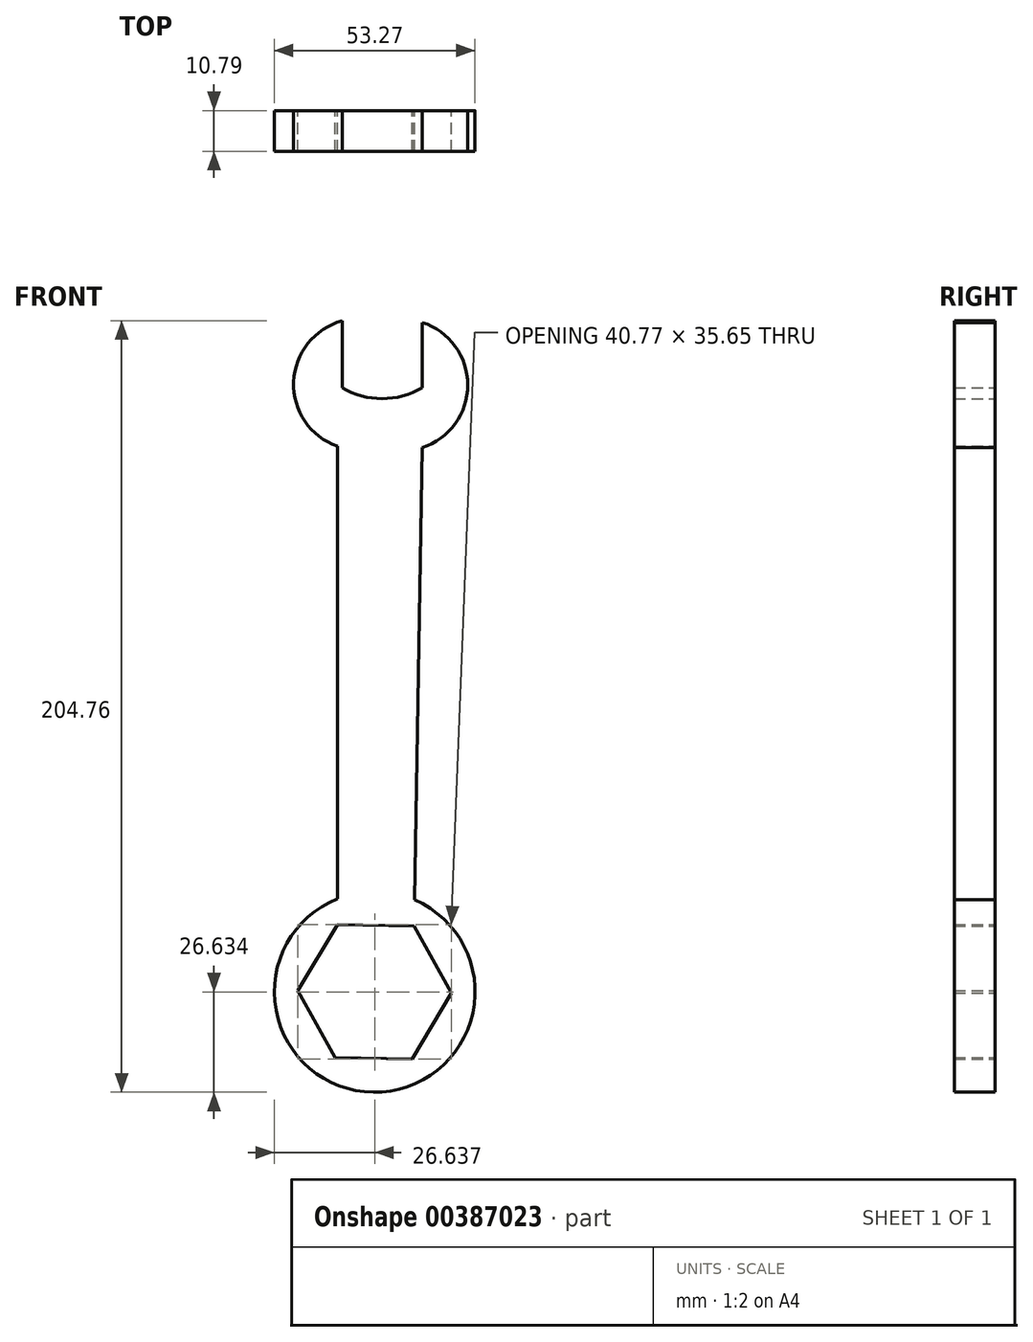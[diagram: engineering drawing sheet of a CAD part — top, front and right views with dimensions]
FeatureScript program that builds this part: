
annotation { "Feature Type Name" : "Feature", "Feature Type Description" : "" }
export const myFeature = defineFeature(function(context is Context, id is Id, definition is map)
    precondition{}
    {
        {
            var Q0;
            Q0=qCreatedBy(makeId("Front.planeOp"),FACE);
            var sketch = newSketch(context, id + "F0", { "sketchPlane" : qUnion([Q0])});
            skCircle(sketch, "E0.cCircle", {"center": v(-38.18, -47.33) * mm, "radius": 17.66 * mm, "construction": true});
            skLineSegment(sketch, "E0.0", {"start": v(-17.8, -47.67) * mm, "end": v(-28.29, -65.15) * mm});
            skLineSegment(sketch, "E0.1", {"start": v(-28.29, -65.15) * mm, "end": v(-48.67, -64.8) * mm});
            skLineSegment(sketch, "E0.2", {"start": v(-48.67, -64.8) * mm, "end": v(-58.57, -46.98) * mm});
            skLineSegment(sketch, "E0.3", {"start": v(-58.57, -46.98) * mm, "end": v(-48.08, -29.5) * mm});
            skLineSegment(sketch, "E0.4", {"start": v(-48.08, -29.5) * mm, "end": v(-27.7, -29.84) * mm});
            skLineSegment(sketch, "E0.5", {"start": v(-27.7, -29.84) * mm, "end": v(-17.8, -47.67) * mm});
            skPoint(sketch, "E0.0.midPoint", {"position": v(-23.04, -56.41) * mm});
            skLineSegment(sketch, "E1", {"start": v(-27.7, -29.84) * mm, "end": v(-25.56, 97.14) * mm});
            skLineSegment(sketch, "E2", {"start": v(-48.08, -29.5) * mm, "end": v(-48.08, 97.5) * mm});
            skCircle(sketch, "E3", {"center": v(-38.18, -47.33) * mm, "radius": 26.63 * mm});
            skArc(sketch, "E4", {"start": v(-25.56, 97.14) * mm, "mid": v(-13.49, 113.75) * mm, "end": v(-25.56, 130.36) * mm});
            skLineSegment(sketch, "E5", {"start": v(-25.56, 130.36) * mm, "end": v(-25.56, 113.06) * mm});
            skArc(sketch, "E6", {"start": v(-46.84, 113.06) * mm, "mid": v(-36.2, 110.14) * mm, "end": v(-25.56, 113.06) * mm});
            skLineSegment(sketch, "E7", {"start": v(-46.84, 113.06) * mm, "end": v(-46.84, 130.8) * mm});
            skArc(sketch, "E8", {"start": v(-46.84, 130.8) * mm, "mid": v(-59.7, 114.6) * mm, "end": v(-48.08, 97.5) * mm});
            skLineSegment(sketch, "E9", {"start": v(-48.08, 97.5) * mm, "end": v(-25.56, 97.14) * mm});
            skSolve(sketch);
        }
        {
            var Q0;
            Q0=makeQuery(id+"F0.imprint","IMPRINT",FACE,{"disambiguationData":[TD([[makeQuery(id+"F0.imprint","IMPRINT",EDGE,{"derivedFrom":sQuery(id+"F0.wireOp",EDGE,"E4")}),1.0]])]});
            extrude(context, id + "F1", {"entities" : qUnion([Q0]), "depth" : 9.02 * mm});
        }
        {
            var Q0;
            Q0 = qSketchRegion(id + "F0", true);
            extrude(context, id + "F2", {"entities" : qUnion([Q0]), "operationType" : NewBodyOperationType.ADD, "depth" : 10.8 * mm});
        }
    });
